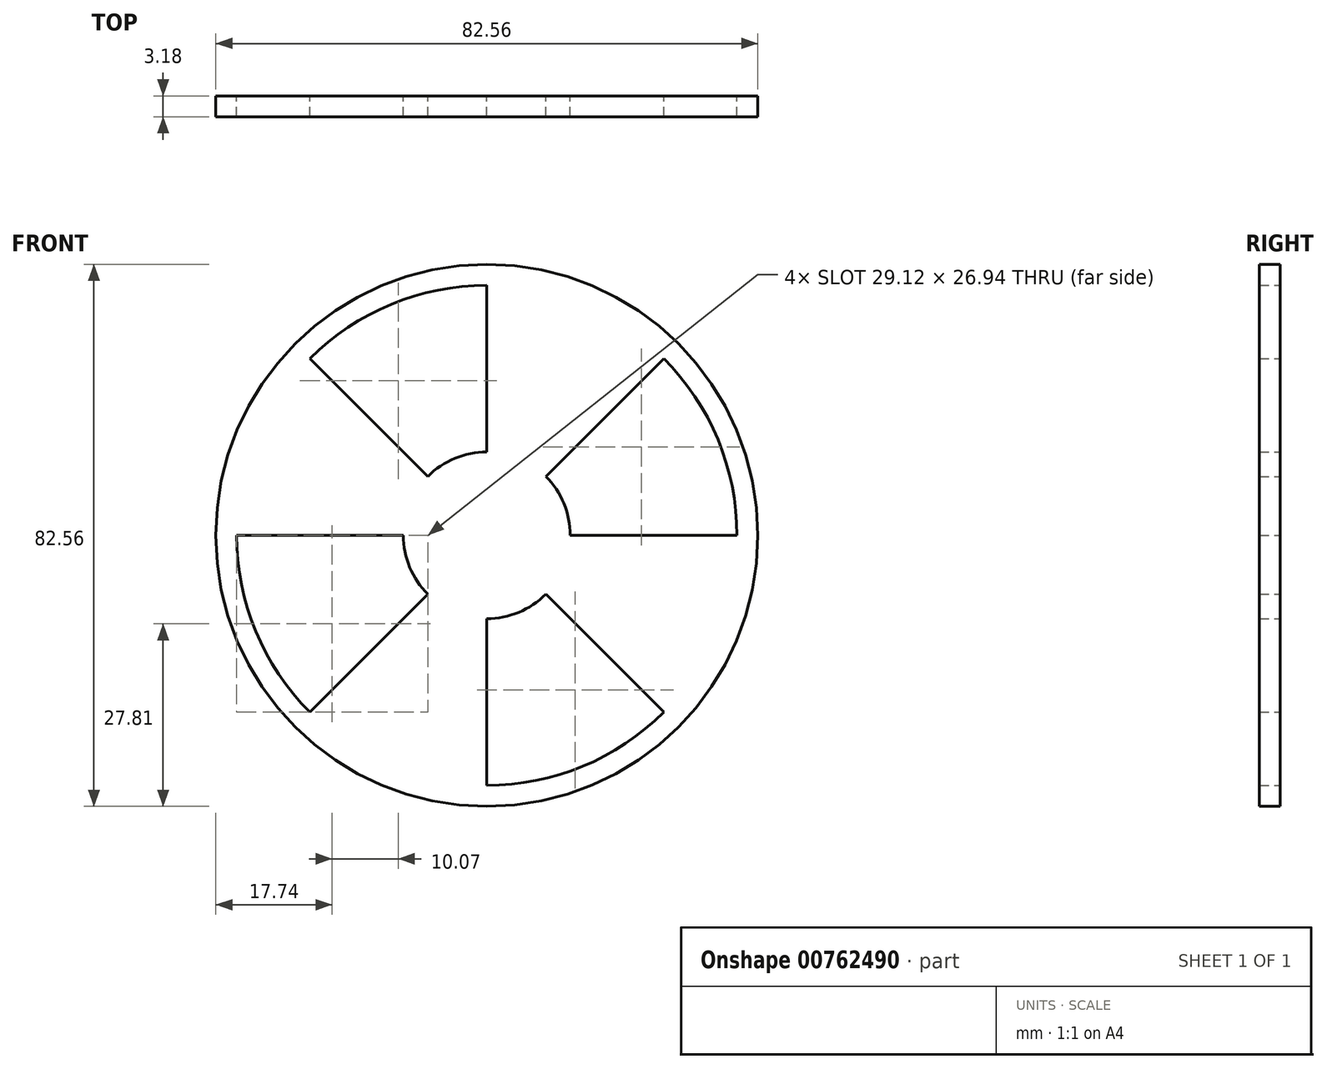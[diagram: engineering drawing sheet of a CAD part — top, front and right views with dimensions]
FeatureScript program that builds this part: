
annotation { "Feature Type Name" : "Feature", "Feature Type Description" : "" }
export const myFeature = defineFeature(function(context is Context, id is Id, definition is map)
    precondition{}
    {
        {
            var Q0;
            Q0=qCreatedBy(makeId("Front.planeOp"),FACE);
            var sketch = newSketch(context, id + "F0", { "sketchPlane" : qUnion([Q0])});
            skCircle(sketch, "E0", {"center": v(0, 0) * mm, "radius": 38.1 * mm});
            skCircle(sketch, "E1", {"center": v(0, 0) * mm, "radius": 9.53 * mm});
            skLineSegment(sketch, "E2", {"start": v(-38.1, 0) * mm, "end": v(-12.7, 0) * mm});
            skLineSegment(sketch, "E3", {"start": v(0, -12.7) * mm, "end": v(0, -38.1) * mm});
            skLineSegment(sketch, "E4", {"start": v(12.7, 0) * mm, "end": v(38.1, 0) * mm});
            skCircle(sketch, "E5", {"center": v(0, 0) * mm, "radius": 12.7 * mm});
            skCircle(sketch, "E6", {"center": v(0, 0) * mm, "radius": 41.28 * mm});
            skLineSegment(sketch, "E7", {"start": v(-8.98, 8.98) * mm, "end": v(-26.94, 26.94) * mm});
            skLineSegment(sketch, "E8", {"start": v(8.98, 8.98) * mm, "end": v(26.94, 26.94) * mm});
            skLineSegment(sketch, "E9", {"start": v(8.98, -8.98) * mm, "end": v(26.94, -26.94) * mm});
            skLineSegment(sketch, "E10", {"start": v(-8.98, -8.98) * mm, "end": v(-26.94, -26.94) * mm});
            skLineSegment(sketch, "E11", {"start": v(0, 12.7) * mm, "end": v(0, 41.28) * mm});
            skSolve(sketch);
        }
        {
            var Q0;
            {var subQ0=sQuery(id+"F0.wireOp",EDGE,"E8");Q0=makeQuery(id+"F0.imprint","IMPRINT",FACE,{"disambiguationData":[TD([[makeQuery(id+"F0.imprint","IMPRINT",EDGE,{"derivedFrom":subQ0}),1.0]])]});}
            var Q1;
            {var subQ0=sQuery(id+"F0.wireOp",EDGE,"E4");Q1=makeQuery(id+"F0.imprint","IMPRINT",FACE,{"disambiguationData":[TD([[makeQuery(id+"F0.imprint","IMPRINT",EDGE,{"derivedFrom":subQ0}),-1.0]])]});}
            var Q2;
            {var subQ0=sQuery(id+"F0.wireOp",EDGE,"E2");Q2=makeQuery(id+"F0.imprint","IMPRINT",FACE,{"disambiguationData":[TD([[makeQuery(id+"F0.imprint","IMPRINT",EDGE,{"derivedFrom":subQ0}),1.0]])]});}
            var Q3;
            {var subQ0=sQuery(id+"F0.wireOp",EDGE,"E3");Q3=makeQuery(id+"F0.imprint","IMPRINT",FACE,{"disambiguationData":[TD([[makeQuery(id+"F0.imprint","IMPRINT",EDGE,{"derivedFrom":subQ0}),-1.0]])]});}
            var Q4;
            {var subQ9=sQuery(id+"F0.wireOp",EDGE,"E6");Q4=makeQuery(id+"F0.imprint","IMPRINT",FACE,{"disambiguationData":[TD([[makeQuery(id+"F0.imprint","IMPRINT",EDGE,{"disambiguationData":[TD([[makeQuery(id+"F0.imprint","IMPRINT",VERTEX,{"derivedFrom":subQ9}),-1.0]])],"derivedFrom":subQ9}),1.0]])]});}
            var Q5;
            Q5=makeQuery(id+"F0.imprint","IMPRINT",FACE,{"disambiguationData":[TD([[makeQuery(id+"F0.imprint","IMPRINT",EDGE,{"derivedFrom":sQuery(id+"F0.wireOp",EDGE,"E1")}),-1.0]])]});
            var Q6;
            Q6=makeQuery(id+"F0.imprint","IMPRINT",FACE,{"disambiguationData":[TD([[makeQuery(id+"F0.imprint","IMPRINT",EDGE,{"derivedFrom":sQuery(id+"F0.wireOp",EDGE,"E1")}),1.0]])]});
            extrude(context, id + "F1", {"entities" : qUnion([Q0, Q1, Q2, Q3, Q4, Q5, Q6]), "depth" : 3.17 * mm, "offsetDistance" : 25.4 * mm});
        }
    });
